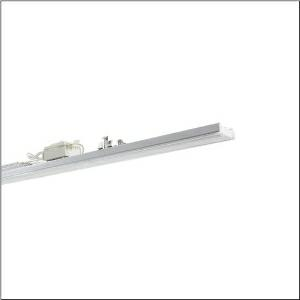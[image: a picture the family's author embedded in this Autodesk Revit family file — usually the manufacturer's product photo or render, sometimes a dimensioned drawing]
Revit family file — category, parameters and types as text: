
# Revit family: licross_r__11_recessed_mo_51tl12dn195g_89b2
name_source: partatom
category: Lighting Fixtures
units: mm (PartAtom-declared; Revit-internal decimal feet)

## family parameters
Cut with Voids When Loaded = No
Host = Face
Light Source = No
Part Type = Normal
Room Calculation Point = No
Round Connector Dimension = Use Diameter
Shared = No

## types (1)
- --- (1 x LED, 9910 lm, 56.7 W, 3500K)
    Apparent Load = 57 VA
    CIE Flux Codes = 67 92 99 100 100
    Color Rendering = 80
    Color Temperature = 3500K
    Default Elevation = 1800 mm
    Description = Licross® 11 Recessed MO, luminaire insert, of sheet steel, coil coated, white, length: 1.500mm, width: 66mm, height: 67mm, LED rated luminous flux: 9.910lm, light colour: 835, control gear: DALI 2, with plug, 5-pole, with phase selection, mains connection: 220..240V, AC, 50/60Hz, rated input power: 57W, halogen-free wiring, primary optical cover: cover, of PMMA, light emission: direct distribution, primary light characteristic: symmetric, protection rating (complete): IP40, insulation class (complete): insulation class I (protective earthing), certification: CE, ENEC, VDE, UKCA, protection symbol: D if used in an environment without relevant dust loads with corresponding accessories, impact resistance: IK06, permissible ambient temperature for indoor applications: -25..+35°C, corresponds to IFS (International Featured Standards) requirements for safety and quality in the food industry, reducing of maximum allowable ambient temperature of 5°C with ceiling mounting, LABS conformity tested according to VDMA 24364:2018-05, packaging unit: 1 piece
    Height = 58 mm
    Lamp = 1 x LED
    Lamp Light Flux = 9910 lm
    Lamp Power = 56.7 W
    Lamp count = 1
    Length = 1500 mm
    Luminous efficacy = 175 lm/W
    Manufacturer = Siteco
    ModVariant = No
    Model = 51TL12DN195G
    Mounting Place = Ceiling
    Mounting Type = Pendant
    Number of Poles = 1
    OnlyDefault = Yes
    Power Factor = 1
    Product Name = Licross® 11 Recessed MO
    Product group = luminaire insert
    ProductGroupID = 902
    Protection Class = Protection class I
    Protection Degree = IP 40
    RLX_Detail_Level = 1
    RLX_Emergency_Light_Flux = 0 lm
    RLX_Emergency_Type = 0
    RLX_Emergency_Type_DB = No
    RlxData = <blob elided: 24337 chars, md5=3ac55d9f>
    Socket = socket
    Standby Power = 0 W
    System Light Flux = 9910 lm
    System Power = 57 W
    Type Comments = factory setting: luminous flux: 100 % | dim-lin: 254 | 378 mA
    Type Image = l_1296930.jpg
    URL = http://relux.com
    VarID = @adj_068160
    Voltage = 0 V
    Weight = 0.00 kg
    Width = 66 mm

## geometry (parser evidence)
native form markers: Blend x4, Sweep x10
no freeform markers — native parametric forms only
